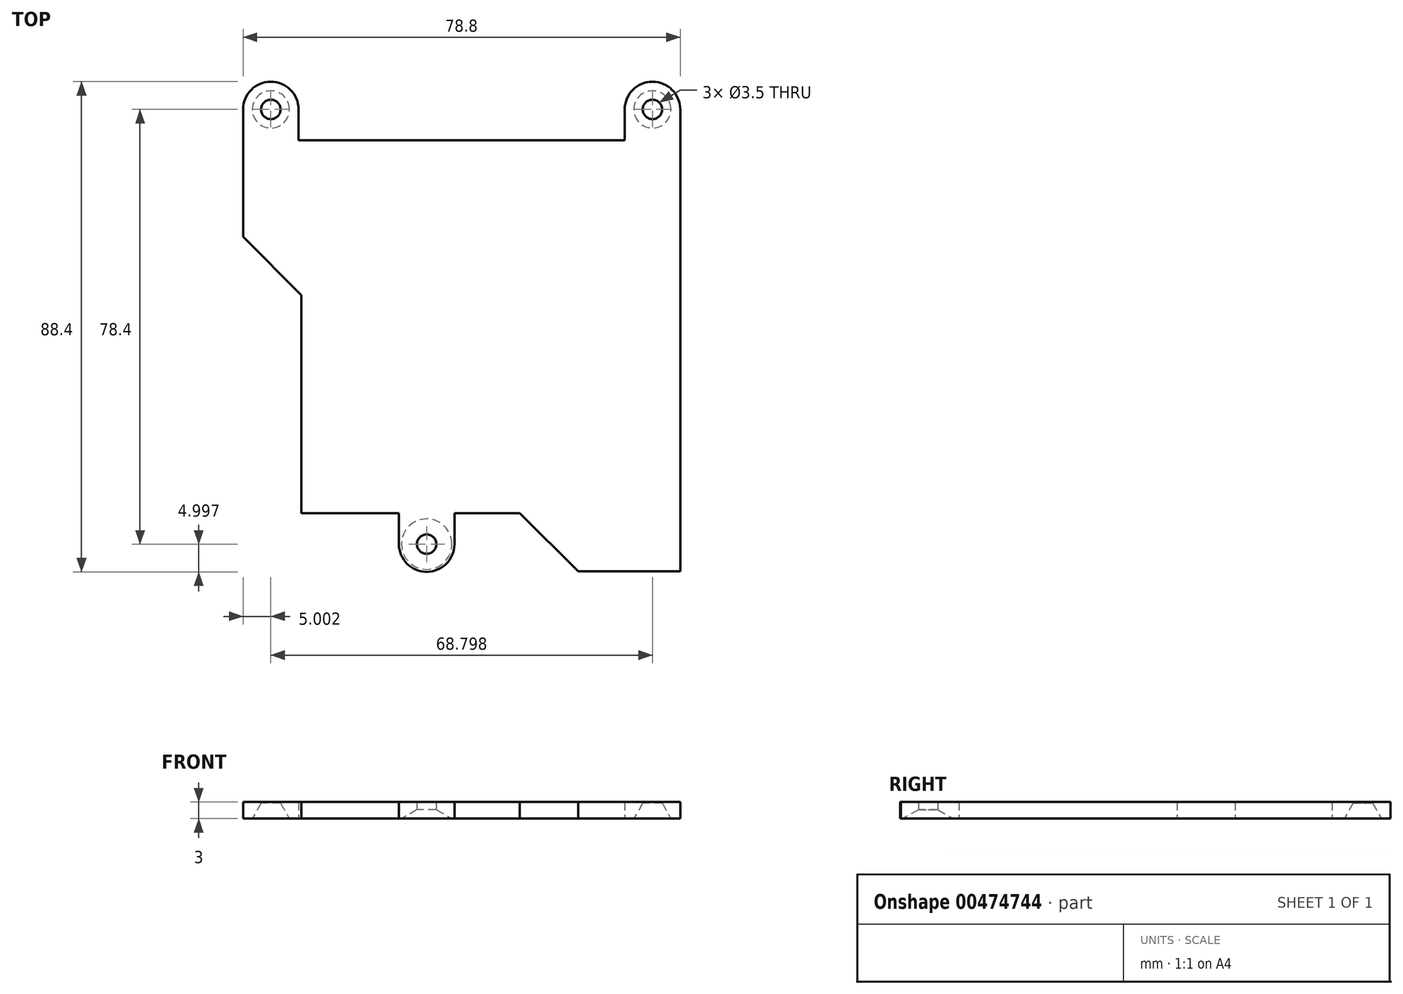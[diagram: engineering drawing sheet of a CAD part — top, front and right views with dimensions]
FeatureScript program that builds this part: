
annotation { "Feature Type Name" : "Feature", "Feature Type Description" : "" }
export const myFeature = defineFeature(function(context is Context, id is Id, definition is map)
    precondition{}
    {
        {
            var Q0;
            Q0=qCreatedBy(makeId("Top.planeOp"),FACE);
            var sketch = newSketch(context, id + "F0", { "sketchPlane" : qUnion([Q0])});
            skLineSegment(sketch, "E0", {"start": v(0, 0) * mm, "end": v(0, -39.5) * mm, "construction": true});
            skLineSegment(sketch, "E1", {"start": v(0, -39.5) * mm, "end": v(17.6, -39.5) * mm, "construction": true});
            skLineSegment(sketch, "E2", {"start": v(39.56, -39.5) * mm, "end": v(50.07, -50) * mm, "construction": true});
            skLineSegment(sketch, "E3", {"start": v(50.07, -50) * mm, "end": v(68.9, -50) * mm, "construction": true});
            skLineSegment(sketch, "E4", {"start": v(68.9, -50) * mm, "end": v(68.9, 33.6) * mm, "construction": true});
            skLineSegment(sketch, "E5", {"start": v(58.3, 28.3) * mm, "end": v(0.1, 28.3) * mm, "construction": true});
            skLineSegment(sketch, "E6", {"start": v(-10.5, 33.6) * mm, "end": v(-10.5, 10.48) * mm, "construction": true});
            skLineSegment(sketch, "E7", {"start": v(-10.5, 10.48) * mm, "end": v(0, 0) * mm, "construction": true});
            skCircle(sketch, "E8", {"center": v(22.9, -44.8) * mm, "radius": 1.4 * mm, "construction": true});
            skCircle(sketch, "E9", {"center": v(-5.2, 33.6) * mm, "radius": 1.4 * mm, "construction": true});
            skCircle(sketch, "E10", {"center": v(63.6, 33.6) * mm, "radius": 1.4 * mm, "construction": true});
            skLineSegment(sketch, "E11", {"start": v(0.1, 28.3) * mm, "end": v(0.1, 33.6) * mm, "construction": true});
            skArc(sketch, "E12", {"start": v(0.1, 33.6) * mm, "mid": v(-5.2, 38.9) * mm, "end": v(-10.5, 33.6) * mm, "construction": true});
            skLineSegment(sketch, "E13", {"start": v(58.3, 28.3) * mm, "end": v(58.3, 33.6) * mm, "construction": true});
            skArc(sketch, "E14", {"start": v(68.9, 33.6) * mm, "mid": v(63.6, 38.9) * mm, "end": v(58.3, 33.6) * mm, "construction": true});
            skLineSegment(sketch, "E15", {"start": v(17.6, -39.5) * mm, "end": v(17.6, -44.8) * mm, "construction": true});
            skLineSegment(sketch, "E16", {"start": v(28.2, -39.5) * mm, "end": v(28.2, -44.8) * mm, "construction": true});
            skArc(sketch, "E17", {"start": v(17.6, -44.8) * mm, "mid": v(22.9, -50.1) * mm, "end": v(28.2, -44.8) * mm, "construction": true});
            skLineSegment(sketch, "E18.trimOffspring", {"start": v(28.2, -39.5) * mm, "end": v(39.56, -39.5) * mm, "construction": true});
            skCircle(sketch, "E19", {"center": v(22.9, -44.8) * mm, "radius": 1.75 * mm});
            skCircle(sketch, "E20", {"center": v(-5.2, 33.6) * mm, "radius": 1.75 * mm});
            skCircle(sketch, "E21", {"center": v(63.6, 33.6) * mm, "radius": 1.75 * mm});
            skLineSegment(sketch, "E22", {"start": v(17.9, -44.8) * mm, "end": v(17.9, -39.2) * mm});
            skLineSegment(sketch, "E23", {"start": v(17.9, -39.2) * mm, "end": v(0.3, -39.2) * mm});
            skLineSegment(sketch, "E24", {"start": v(27.9, -44.8) * mm, "end": v(27.9, -39.2) * mm});
            skArc(sketch, "E25", {"start": v(17.9, -44.8) * mm, "mid": v(22.9, -49.8) * mm, "end": v(27.9, -44.8) * mm});
            skLineSegment(sketch, "E26", {"start": v(0.3, -39.2) * mm, "end": v(0.3, 0.12) * mm});
            skLineSegment(sketch, "E27", {"start": v(0.3, 0.12) * mm, "end": v(-10.2, 10.6) * mm});
            skLineSegment(sketch, "E28", {"start": v(-10.2, 10.6) * mm, "end": v(-10.2, 33.6) * mm});
            skArc(sketch, "E29", {"start": v(-0.2, 33.6) * mm, "mid": v(-5.2, 38.6) * mm, "end": v(-10.2, 33.6) * mm});
            skLineSegment(sketch, "E30", {"start": v(-0.2, 33.6) * mm, "end": v(-0.2, 28) * mm});
            skLineSegment(sketch, "E31", {"start": v(-0.2, 28) * mm, "end": v(58.6, 28) * mm});
            skLineSegment(sketch, "E32", {"start": v(27.9, -39.2) * mm, "end": v(39.68, -39.2) * mm});
            skLineSegment(sketch, "E33", {"start": v(39.68, -39.2) * mm, "end": v(50.2, -49.7) * mm});
            skLineSegment(sketch, "E34", {"start": v(50.2, -49.7) * mm, "end": v(68.6, -49.7) * mm});
            skLineSegment(sketch, "E35", {"start": v(68.6, -49.7) * mm, "end": v(68.6, 33.6) * mm});
            skArc(sketch, "E36", {"start": v(68.6, 33.6) * mm, "mid": v(63.6, 38.6) * mm, "end": v(58.6, 33.6) * mm});
            skLineSegment(sketch, "E37", {"start": v(58.6, 33.6) * mm, "end": v(58.6, 28) * mm});
            skSolve(sketch);
        }
        {
            var Q0;
            Q0 = qSketchRegion(id + "F0", true);
            extrude(context, id + "F1", {"entities" : qUnion([Q0]), "depth" : 3 * mm, "offsetDistance" : 25 * mm});
        }
        {
            var Q0;
            Q0=makeQuery(id+"F1.opExtrude","CAP_EDGE",EDGE,{"disambiguationData":[OSD([sQuery(id+"F0.wireOp",EDGE,"E19")])],"isStart":true});
            var Q1;
            Q1=makeQuery(id+"F1.opExtrude","CAP_EDGE",EDGE,{"disambiguationData":[OSD([sQuery(id+"F0.wireOp",EDGE,"E20")])],"isStart":true});
            var Q2;
            Q2=makeQuery(id+"F1.opExtrude","CAP_EDGE",EDGE,{"disambiguationData":[OSD([sQuery(id+"F0.wireOp",EDGE,"E21")])],"isStart":true});
            chamfer(context, id + "F2", {"entities" : qUnion([Q0, Q1, Q2]), "chamferType" : ChamferType.TWO_OFFSETS, "width1" : 1.6 * mm, "oppositeDirection" : false, "width2" : 2.8 * mm, "tangentPropagation" : true});
        }
    });
